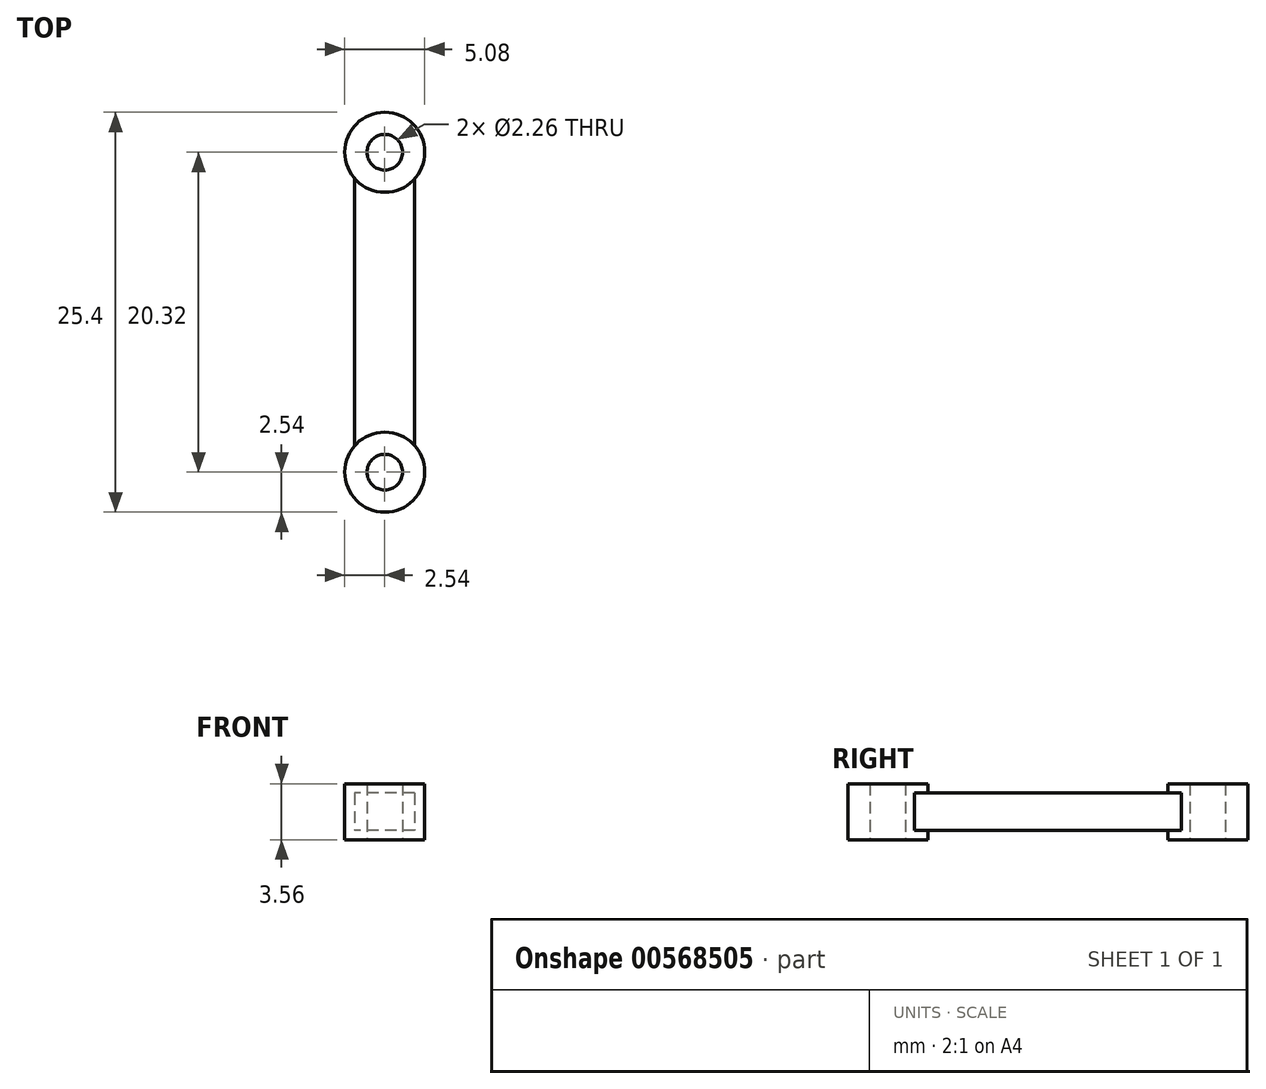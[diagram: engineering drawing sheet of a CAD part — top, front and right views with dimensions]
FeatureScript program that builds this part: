
annotation { "Feature Type Name" : "Feature", "Feature Type Description" : "" }
export const myFeature = defineFeature(function(context is Context, id is Id, definition is map)
    precondition{}
    {
        {
            var Q0;
            Q0=qCreatedBy(makeId("Top.planeOp"),FACE);
            var sketch = newSketch(context, id + "F0", { "sketchPlane" : qUnion([Q0])});
            skLineSegment(sketch, "E0", {"start": v(0, 0) * mm, "end": v(0, -10.16) * mm});
            skLineSegment(sketch, "E1", {"start": v(0, -10.16) * mm, "end": v(0, 10.16) * mm});
            skCircle(sketch, "E2", {"center": v(0, 10.16) * mm, "radius": 2.54 * mm});
            skCircle(sketch, "E3", {"center": v(0, -10.16) * mm, "radius": 2.54 * mm});
            skLineSegment(sketch, "E4", {"start": v(-1.9, 8.48) * mm, "end": v(-1.9, -8.48) * mm});
            skLineSegment(sketch, "E5", {"start": v(1.9, 8.48) * mm, "end": v(1.9, -8.48) * mm});
            skSolve(sketch);
        }
        {
            var Q0;
            {var subQ0=sQuery(id+"F0.wireOp",EDGE,"E4");Q0=makeQuery(id+"F0.imprint","IMPRINT",FACE,{"disambiguationData":[TD([[makeQuery(id+"F0.imprint","IMPRINT",EDGE,{"derivedFrom":subQ0}),1.0]])]});}
            var Q1;
            {var subQ0=sQuery(id+"F0.wireOp",EDGE,"E5");Q1=makeQuery(id+"F0.imprint","IMPRINT",FACE,{"disambiguationData":[TD([[makeQuery(id+"F0.imprint","IMPRINT",EDGE,{"derivedFrom":subQ0}),-1.0]])]});}
            extrude(context, id + "F1", {"entities" : qUnion([Q0, Q1]), "endBound" : BoundingType.SYMMETRIC, "depth" : 2.36 * mm, "offsetDistance" : 25.4 * mm});
        }
        {
            var Q0;
            Q0=qCreatedBy(makeId("Top.planeOp"),FACE);
            var sketch = newSketch(context, id + "F2", { "sketchPlane" : qUnion([Q0])});
            skLineSegment(sketch, "E6", {"start": v(0, 0) * mm, "end": v(0, 10.16) * mm});
            skLineSegment(sketch, "E7", {"start": v(0, 10.16) * mm, "end": v(0, -10.16) * mm});
            skCircle(sketch, "E8", {"center": v(0, -10.16) * mm, "radius": 2.54 * mm});
            skCircle(sketch, "E9", {"center": v(0, 10.16) * mm, "radius": 2.54 * mm});
            skCircle(sketch, "E10", {"center": v(0, 10.16) * mm, "radius": 1.13 * mm});
            skCircle(sketch, "E11", {"center": v(0, -10.16) * mm, "radius": 1.13 * mm});
            skSolve(sketch);
        }
        {
            var Q0;
            Q0 = qSketchRegion(id + "F2", true);
            extrude(context, id + "F3", {"entities" : qUnion([Q0]), "operationType" : NewBodyOperationType.ADD, "endBound" : BoundingType.SYMMETRIC, "depth" : 3.56 * mm, "offsetDistance" : 25.4 * mm});
        }
    });
